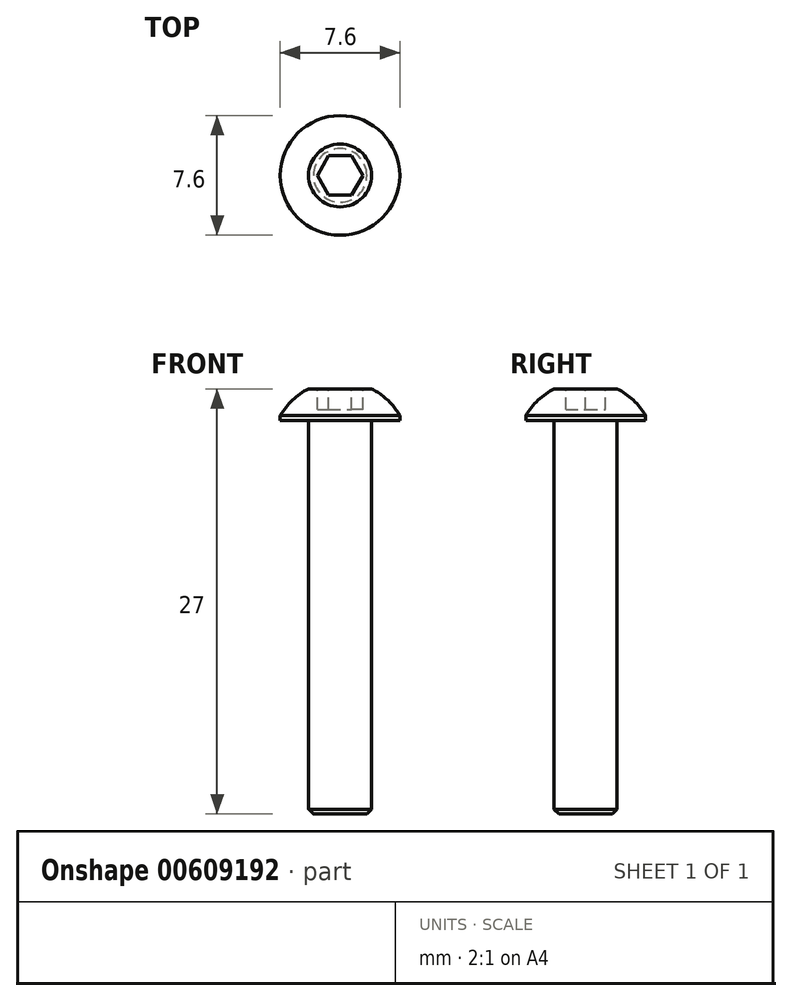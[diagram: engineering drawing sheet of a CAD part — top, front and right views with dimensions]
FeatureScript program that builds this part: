
annotation { "Feature Type Name" : "Feature", "Feature Type Description" : "" }
export const myFeature = defineFeature(function(context is Context, id is Id, definition is map)
    precondition{}
    {
        {
            var Q0;
            Q0=qCreatedBy(makeId("Front.planeOp"),FACE);
            var sketch = newSketch(context, id + "F0", { "sketchPlane" : qUnion([Q0])});
            skLineSegment(sketch, "E0.top", {"start": v(-3.8, -0.3) * mm, "end": v(0, -0.3) * mm});
            skLineSegment(sketch, "E0.left", {"start": v(-3.8, 0) * mm, "end": v(-3.8, -0.3) * mm});
            skLineSegment(sketch, "E1", {"start": v(-2, 1.7) * mm, "end": v(0, 1.7) * mm});
            skArc(sketch, "E2.trimOffspring", {"start": v(-2, 1.7) * mm, "mid": v(-3.02, 0.98) * mm, "end": v(-3.8, 0) * mm});
            skLineSegment(sketch, "E3", {"start": v(0, 1.7) * mm, "end": v(0, -0.3) * mm});
            skSolve(sketch);
        }
        {
            var Q0;
            Q0 = qSketchRegion(id + "F0", true);
            var Q1;
            Q1=sQuery(id+"F0.wireOp",EDGE,"E3");
            revolve(context, id + "F1", {"entities" : qUnion([Q0]), "axis" : qUnion([Q1]), "revolveType" : RevolveType.FULL});
        }
        {
            var Q0;
            Q0=makeQuery(id+"F1.opRevolve","SWEPT_FACE",FACE,{"disambiguationData":[OSD([sQuery(id+"F0.wireOp",EDGE,"E1")])]});
            var sketch = newSketch(context, id + "F2", { "sketchPlane" : qUnion([Q0])});
            skCircle(sketch, "E4.cCircle", {"center": v(0, 0) * mm, "radius": 1.25 * mm, "construction": true});
            skLineSegment(sketch, "E4.0", {"start": v(-0.72, 1.25) * mm, "end": v(0.72, 1.25) * mm});
            skLineSegment(sketch, "E4.1", {"start": v(0.72, 1.25) * mm, "end": v(1.44, 0) * mm});
            skLineSegment(sketch, "E4.2", {"start": v(1.44, 0) * mm, "end": v(0.72, -1.25) * mm});
            skLineSegment(sketch, "E4.3", {"start": v(0.72, -1.25) * mm, "end": v(-0.72, -1.25) * mm});
            skLineSegment(sketch, "E4.4", {"start": v(-0.72, -1.25) * mm, "end": v(-1.44, 0) * mm});
            skLineSegment(sketch, "E4.5", {"start": v(-1.44, 0) * mm, "end": v(-0.72, 1.25) * mm});
            skPoint(sketch, "E4.0.midPoint", {"position": v(0, 1.25) * mm});
            skSolve(sketch);
        }
        {
            var Q0;
            Q0 = qSketchRegion(id + "F2", true);
            extrude(context, id + "F3", {"entities" : qUnion([Q0]), "operationType" : NewBodyOperationType.REMOVE, "oppositeDirection" : true, "depth" : 1.3 * mm, "offsetDistance" : 25 * mm});
        }
        {
            var Q0;
            Q0=makeQuery(id+"F1.opRevolve","SWEPT_FACE",FACE,{"disambiguationData":[OSD([sQuery(id+"F0.wireOp",EDGE,"E0.top")])]});
            var sketch = newSketch(context, id + "F4", { "sketchPlane" : qUnion([Q0])});
            skCircle(sketch, "E5", {"center": v(0, 0) * mm, "radius": 2 * mm});
            skSolve(sketch);
        }
        {
            var Q0;
            Q0 = qSketchRegion(id + "F4", true);
            extrude(context, id + "F5", {"entities" : qUnion([Q0]), "operationType" : NewBodyOperationType.ADD, "depth" : 25 * mm, "offsetDistance" : 25 * mm});
        }
        {
            var Q0;
            Q0=makeQuery(id+"F5.opExtrude","CAP_EDGE",EDGE,{"disambiguationData":[OSD([sQuery(id+"F4.wireOp",EDGE,"E5")])],"isStart":false});
            chamfer(context, id + "F6", {"entities" : qUnion([Q0]), "width" : 0.3 * mm, "tangentPropagation" : true});
        }
    });
